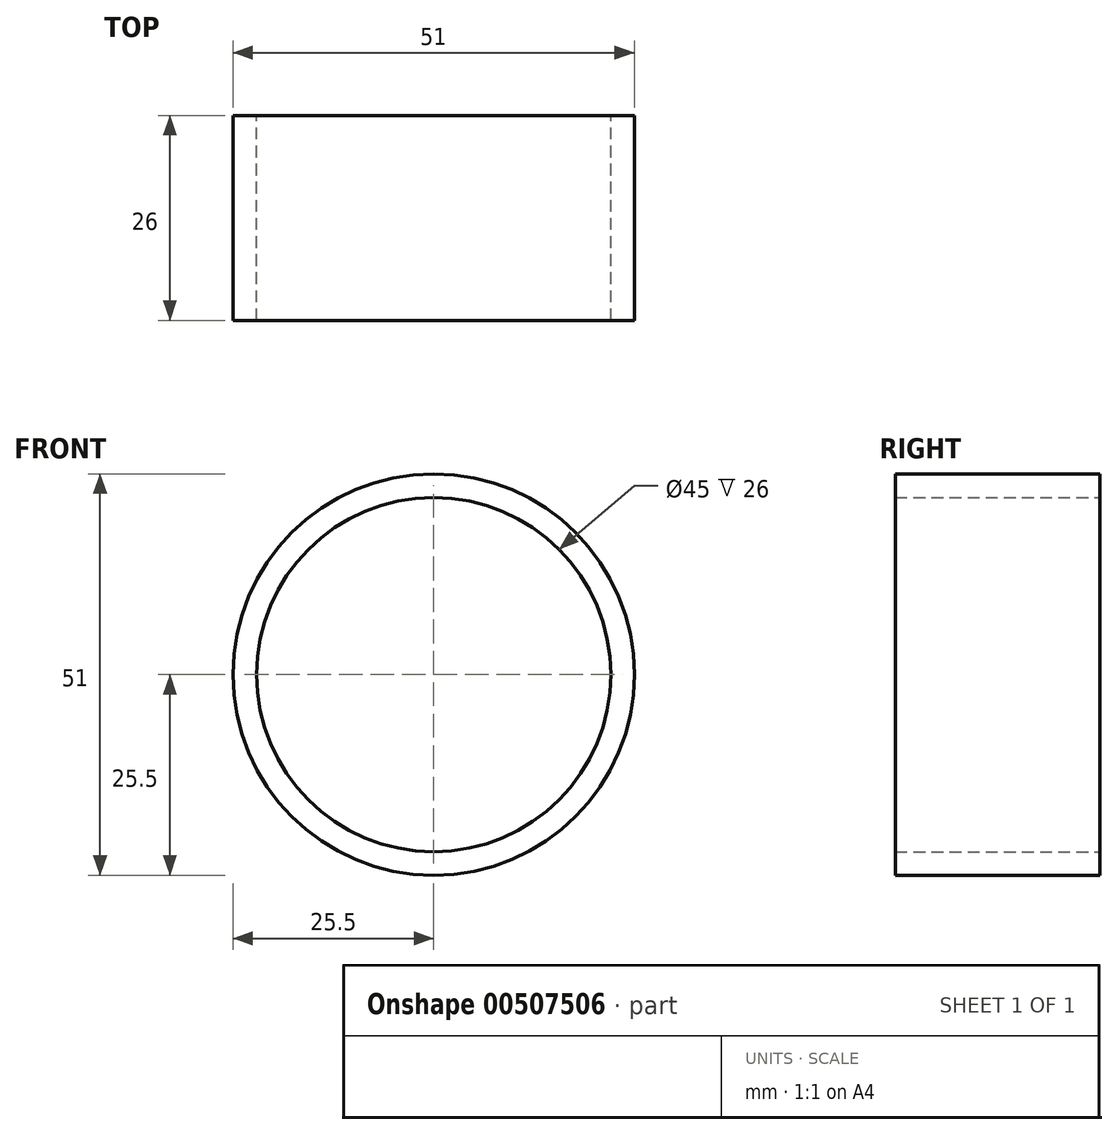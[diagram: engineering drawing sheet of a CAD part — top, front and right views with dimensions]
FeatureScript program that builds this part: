
annotation { "Feature Type Name" : "Feature", "Feature Type Description" : "" }
export const myFeature = defineFeature(function(context is Context, id is Id, definition is map)
    precondition{}
    {
        {
            var Q0;
            Q0=qCreatedBy(makeId("Front.planeOp"),FACE);
            var sketch = newSketch(context, id + "F0", { "sketchPlane" : qUnion([Q0])});
            skCircle(sketch, "E0", {"center": v(0, 0) * mm, "radius": 25.5 * mm});
            skCircle(sketch, "E1", {"center": v(0, 0) * mm, "radius": 22.5 * mm});
            skSolve(sketch);
        }
        {
            var Q0;
            Q0=qSketchRegion(id+"F0",true);
            extrude(context, id + "F1", {"entities" : qUnion([Q0]), "depth" : 26 * mm});
        }
    });
